# Revit family: WGH
name_source: partatom
category: Lighting Fixtures
units: mm (PartAtom-declared; Revit-internal decimal feet)

## family parameters
Cut with Voids When Loaded = No
Host = Face
Light Source = Yes
OmniClass Number = 23.80.70.14
OmniClass Title = Luminaries for External Lighting
Part Type = Normal
Room Calculation Point = No
Round Connector Dimension = Use Diameter
Shared = No

## types (1)
- WGH- Medium- BR
    Color Filter = 16777215
    Colour = Dark bronze powder paint
    Default Elevation = 48"
    Description = Perimeter lighting for safety and security. 
Use on factories, warehouses, self storage , commercial buildings etc.
    Dimming Lamp Color Temperature Shift = <None>
    Emit from Line Length = 6"
    Glass = Glass
    Lamp = 1
    Light Source Symbol Size = 3"
    Light source = 0 lx
    Manufacturer = EXO
    Model = WGH
    URL = https://www.currentlighting.com
    Wattage Comments = 100W/100W

## geometry (parser evidence)
native form markers: Blend x19, Sweep x2
no freeform markers — native parametric forms only
